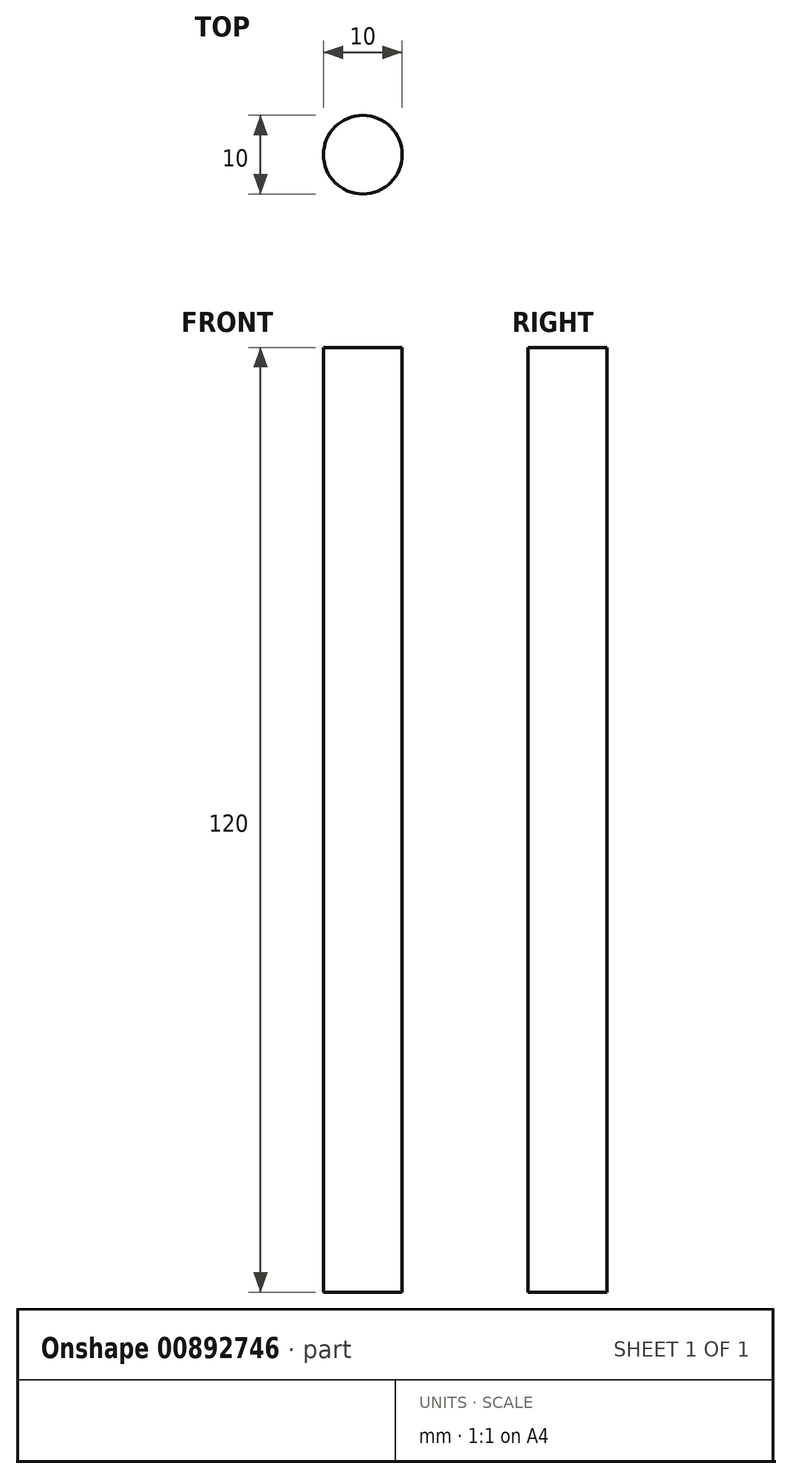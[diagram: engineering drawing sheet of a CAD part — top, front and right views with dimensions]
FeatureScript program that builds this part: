
annotation { "Feature Type Name" : "Feature", "Feature Type Description" : "" }
export const myFeature = defineFeature(function(context is Context, id is Id, definition is map)
    precondition{}
    {
        {
            var Q0;
            Q0=qCreatedBy(makeId("Top.planeOp"),FACE);
            var sketch = newSketch(context, id + "F0", { "sketchPlane" : qUnion([Q0])});
            skCircle(sketch, "E0", {"center": v(0, 0) * mm, "radius": 5 * mm});
            skSolve(sketch);
        }
        {
            var Q0;
            Q0 = qSketchRegion(id + "F0", true);
            extrude(context, id + "F1", {"entities" : qUnion([Q0]), "depth" : 120 * mm, "offsetDistance" : 25 * mm});
        }
    });
